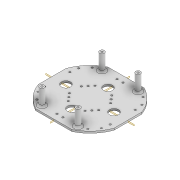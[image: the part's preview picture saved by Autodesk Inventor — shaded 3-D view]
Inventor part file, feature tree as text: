
AUTODESK INVENTOR PART (.ipt)
format: ipt  version: 2022 (Build 260153000, 153)  size: 254,976 bytes
history: native  units: mm
features: extrude x5, mirror x3, plane x2, sketch x2, fillet x1, projected_geometry x1
ambient origin geometry x8: Origin, YZ Plane, XZ Plane, XY Plane, X Axis, Y Axis, Z Axis, Center Point
bodies: Solid1 (feature_tree)
feature tree (14):
  extrude  "Extrusion1"  Depth=3.0mm TaperAngle=0.0deg
  extrude  "Extrusion3"  Depth=3.0mm
  plane  "Work Plane5"
  plane  "Work Plane6"
  mirror  "Mirror3"
  mirror  "Mirror4"
  extrude  "Extrusion4"  Depth=3.0mm
  mirror  "Mirror5"
  sketch  "Sketch9"  dims[d25=60.0mm d27=8.726646mm d28=3.0mm d30=3.0mm d32=25.0mm d33=62.0mm d34=8.0mm d35=8.0mm d36=10.0mm d37=0.0mm d38=63.0mm d39=63.0mm d40=3.0mm d41=25.0mm d42=3.0mm d43=3.0mm d44=10.0mm d45=10.0mm d46=4.95mm d47=4.95mm d48=100.0mm d49=0.0mm d50=3.0mm d51=10.0mm d52=15.0mm d53=40.0mm d54=15.0mm d55=30.0mm d56=8.0mm d57=8.0mm d58=8.0mm d59=8.0mm d60=0.1mm d61=0.1mm d62=0.1mm d63=0.1mm d64=10.0mm d65=0.0mm d66=27.0mm d67=0.0mm d68=3.0mm]
  extrude  "Extrusion5"  Depth=3.0mm
  extrude  "Extrusion6"  Depth=3.0mm
  fillet  "Fillet2"  Radius=62.0mm
  sketch  "Sketch7"  dims[d0=120.0mm d2=3.0mm d3=0.0mm]
  projected_geometry  "Projected Loop5"
